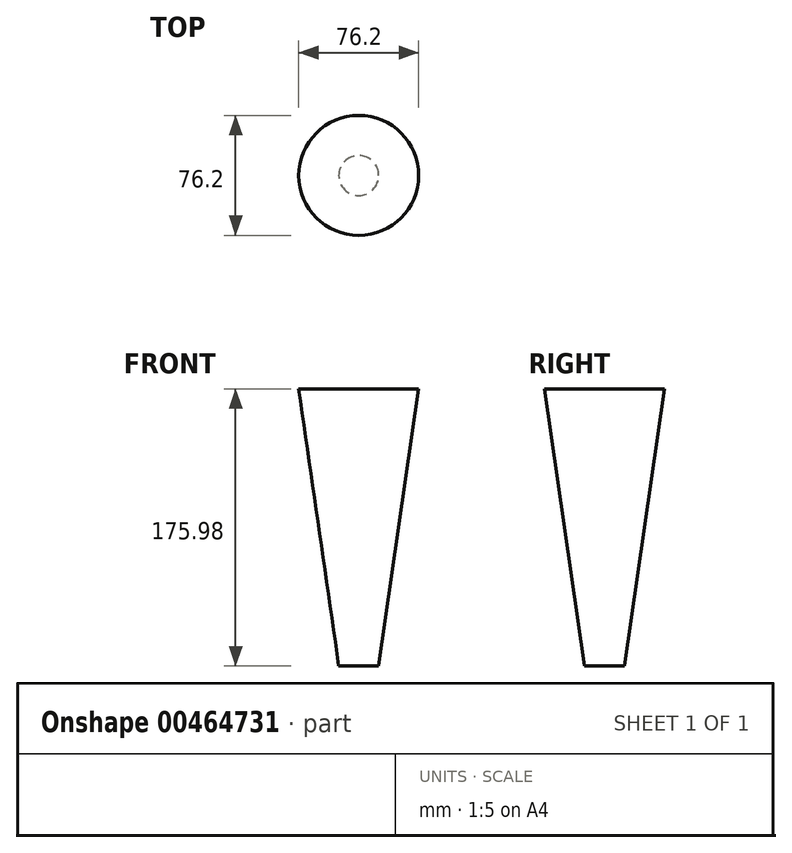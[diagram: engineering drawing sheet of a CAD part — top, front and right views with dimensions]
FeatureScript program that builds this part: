
annotation { "Feature Type Name" : "Feature", "Feature Type Description" : "" }
export const myFeature = defineFeature(function(context is Context, id is Id, definition is map)
    precondition{}
    {
        {
            var Q0;
            Q0=qCreatedBy(makeId("Front.planeOp"),FACE);
            var sketch = newSketch(context, id + "F0", { "sketchPlane" : qUnion([Q0])});
            skLineSegment(sketch, "E0", {"start": v(-38.1, 0) * mm, "end": v(-12.7, -175.98) * mm});
            skLineSegment(sketch, "E1", {"start": v(-12.7, -175.98) * mm, "end": v(0, -175.98) * mm});
            skLineSegment(sketch, "E2", {"start": v(0, -175.98) * mm, "end": v(0, 0) * mm});
            skLineSegment(sketch, "E3", {"start": v(0, 0) * mm, "end": v(-38.1, 0) * mm});
            skSolve(sketch);
        }
        {
            var Q0;
            Q0=makeQuery(id+"F0.imprint","IMPRINT",FACE,{"disambiguationData":[TD([[makeQuery(id+"F0.imprint","IMPRINT",EDGE,{"derivedFrom":sQuery(id+"F0.wireOp",EDGE,"E0")}),1.0]])]});
            var Q1;
            Q1=sQuery(id+"F0.wireOp",EDGE,"E2");
            revolve(context, id + "F1", {"entities" : qUnion([Q0]), "axis" : qUnion([Q1]), "revolveType" : RevolveType.FULL});
        }
    });
